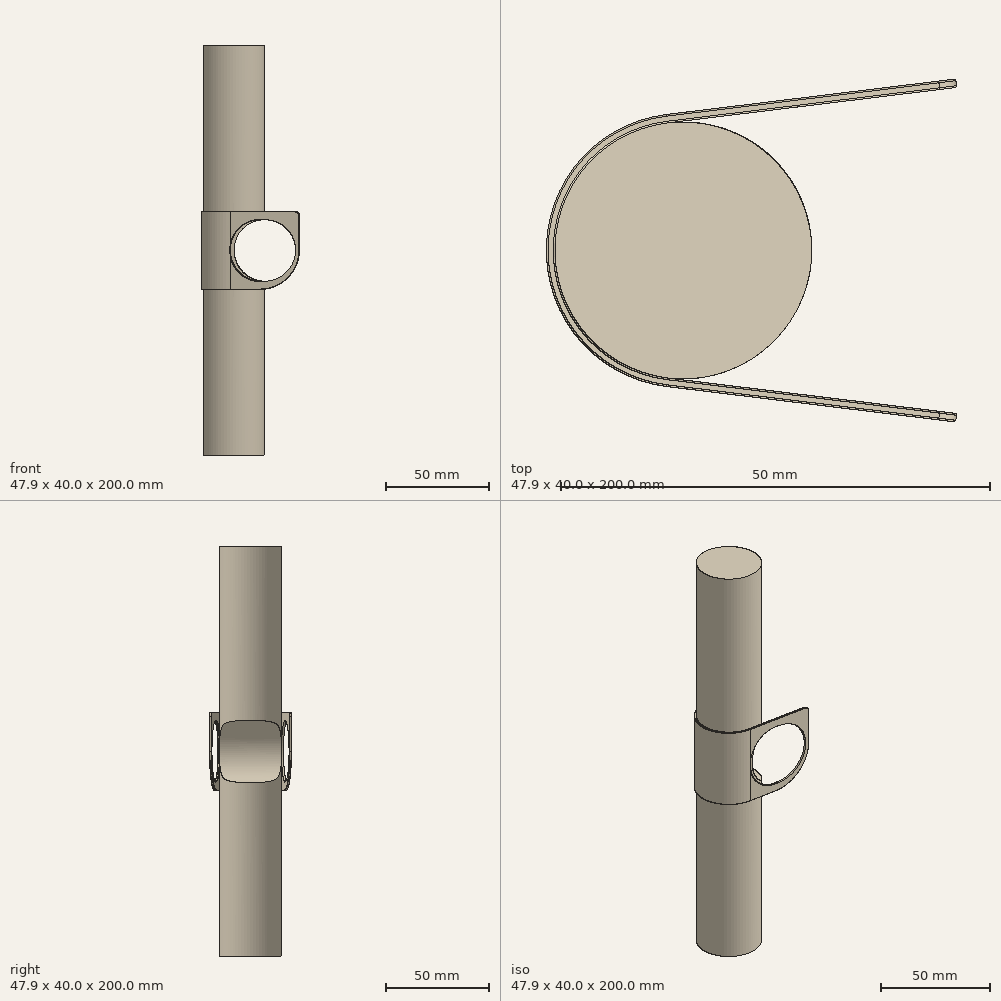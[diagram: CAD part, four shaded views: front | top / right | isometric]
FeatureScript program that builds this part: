
annotation { "Feature Type Name" : "Feature", "Feature Type Description" : "" }
export const myFeature = defineFeature(function(context is Context, id is Id, definition is map)
    precondition{}
    {
        {
            var Q0;
            Q0=qCreatedBy(makeId("Top.planeOp"),FACE);
            var sketch = newSketch(context, id + "F0", { "sketchPlane" : qUnion([Q0])});
            skArc(sketch, "E0", {"start": v(-21.83, 14.89) * mm, "mid": v(-35, 0) * mm, "end": v(-21.83, -14.89) * mm});
            skLineSegment(sketch, "E1", {"start": v(-21.83, 14.89) * mm, "end": v(11.92, 19.03) * mm});
            skLineSegment(sketch, "E2.MirrorCS", {"start": v(-21.83, -14.89) * mm, "end": v(11.92, -19.03) * mm});
            skLineSegment(sketch, "E3.0", {"start": v(-21.95, 15.88) * mm, "end": v(11.8, 20.02) * mm});
            skArc(sketch, "E3.1", {"start": v(-21.95, 15.88) * mm, "mid": v(-36, 0) * mm, "end": v(-21.95, -15.88) * mm});
            skLineSegment(sketch, "E3.2", {"start": v(-21.95, -15.88) * mm, "end": v(11.8, -20.02) * mm});
            skLineSegment(sketch, "E4", {"start": v(11.92, -19.03) * mm, "end": v(11.8, -20.02) * mm});
            skLineSegment(sketch, "E5", {"start": v(11.92, 19.03) * mm, "end": v(11.8, 20.02) * mm});
            skSolve(sketch);
        }
        {
            var Q0;
            Q0 = qSketchRegion(id + "F0", true);
            extrude(context, id + "F1", {"entities" : qUnion([Q0]), "endBound" : BoundingType.SYMMETRIC, "depth" : 38 * mm});
        }
        {
            var Q0;
            Q0=makeQuery(id+"F1.opExtrude","CAP_EDGE",EDGE,{"disambiguationData":[OSD([sQuery(id+"F0.wireOp",EDGE,"E5")])],"isStart":true});
            var Q1;
            Q1=makeQuery(id+"F1.opExtrude","CAP_EDGE",EDGE,{"disambiguationData":[OSD([sQuery(id+"F0.wireOp",EDGE,"E4")])],"isStart":true});
            fillet(context, id + "F2", {"entities" : qUnion([Q0, Q1]), "radius" : 19 * mm, "tangentPropagation" : true, "allowEdgeOverflow" : false});
        }
        {
            var Q0;
            Q0=makeQuery(id+"F1.opExtrude","CAP_EDGE",EDGE,{"disambiguationData":[OSD([sQuery(id+"F0.wireOp",EDGE,"E4")])],"isStart":false});
            var Q1;
            Q1=makeQuery(id+"F1.opExtrude","CAP_EDGE",EDGE,{"disambiguationData":[OSD([sQuery(id+"F0.wireOp",EDGE,"E5")])],"isStart":false});
            fillet(context, id + "F3", {"entities" : qUnion([Q0, Q1]), "radius" : 2 * mm, "tangentPropagation" : true, "allowEdgeOverflow" : false});
        }
        {
            var Q0;
            Q0=makeQuery(id+"F1.opExtrude","SWEPT_EDGE",EDGE,{"disambiguationData":[OSD([sQuery(id+"F0.wireOp",EDGE,"E3.2"),sQuery(id+"F0.wireOp",EDGE,"E4")])]});
            var Q1;
            Q1=makeQuery(id+"F3.opFillet","BLEND_EDGE",EDGE,{"blendedFrom":[makeQuery(id+"F1.opExtrude","CAP_EDGE",EDGE,{"disambiguationData":[OSD([sQuery(id+"F0.wireOp",EDGE,"E4")])],"isStart":false}),makeQuery(id+"F1.opExtrude","SWEPT_FACE",FACE,{"disambiguationData":[OSD([sQuery(id+"F0.wireOp",EDGE,"E2.MirrorCS")])]})],"blendedInto":[makeQuery(id+"F1.opExtrude","SWEPT_FACE",FACE,{"disambiguationData":[OSD([sQuery(id+"F0.wireOp",EDGE,"E2.MirrorCS")])]})]});
            fillet(context, id + "F4", {"entities" : qUnion([Q0, Q1]), "radius" : .2 * mm, "tangentPropagation" : true, "allowEdgeOverflow" : false});
        }
        {
            var Q0;
            Q0=makeQuery(id+"F1.opExtrude","SWEPT_FACE",FACE,{"disambiguationData":[OSD([sQuery(id+"F0.wireOp",EDGE,"E3.2")])]});
            var sketch = newSketch(context, id + "F5", { "sketchPlane" : qUnion([Q0])});
            skCircle(sketch, "E6", {"center": v(-4.85, 0) * mm, "radius": 15 * mm});
            skSolve(sketch);
        }
        {
            var Q0;
            Q0 = qSketchRegion(id + "F5", true);
            extrude(context, id + "F6", {"entities" : qUnion([Q0]), "operationType" : NewBodyOperationType.REMOVE, "oppositeDirection" : true, "depth" : 1 * mm});
        }
        {
            var Q0;
            Q0=makeQuery(id+"F6.boolean.opBoolean","COPY",FACE,{"derivedFrom":makeQuery(id+"F6.opExtrude","SWEPT_FACE",FACE,{"disambiguationData":[OSD([sQuery(id+"F5.wireOp",EDGE,"E6")])]})});
            var Q1;
            Q1=makeQuery(id+"FIFMAnxj8Y7ZVyH_1.1.F6.boolean.opBoolean","COPY",FACE,{"derivedFrom":makeQuery(id+"FIFMAnxj8Y7ZVyH_1.1.F6.opExtrude","SWEPT_FACE",FACE,{"disambiguationData":[OSD([sQuery(id+"F5.wireOp",EDGE,"E6")])]})});
            fillet(context, id + "F7", {"entities" : qUnion([Q0, Q1]), "radius" : .2 * mm, "tangentPropagation" : true, "allowEdgeOverflow" : false});
        }
        {
            var Q0;
            Q0=qCreatedBy(makeId("Top.planeOp"),FACE);
            var sketch = newSketch(context, id + "F8", { "sketchPlane" : qUnion([Q0])});
            skCircle(sketch, "E7", {"center": v(-20, 0) * mm, "radius": 15 * mm});
            skSolve(sketch);
        }
        {
            var Q0;
            Q0 = qSketchRegion(id + "F8", true);
            extrude(context, id + "F9", {"entities" : qUnion([Q0]), "endBound" : BoundingType.SYMMETRIC, "depth" : 200 * mm});
        }
        {
            var Q0;
            Q0=qCreatedBy(makeId("Front.planeOp"),FACE);
            var sketch = newSketch(context, id + "F10", { "sketchPlane" : qUnion([Q0])});
            skCircle(sketch, "E8", {"center": v(-5, 0) * mm, "radius": 15 * mm});
            skSolve(sketch);
        }
        {
            var Q0;
            Q0 = qSketchRegion(id + "F10", true);
            extrude(context, id + "F11", {"entities" : qUnion([Q0]), "operationType" : NewBodyOperationType.REMOVE, "endBound" : BoundingType.SYMMETRIC, "oppositeDirection" : true, "depth" : 40 * mm});
        }
    });
